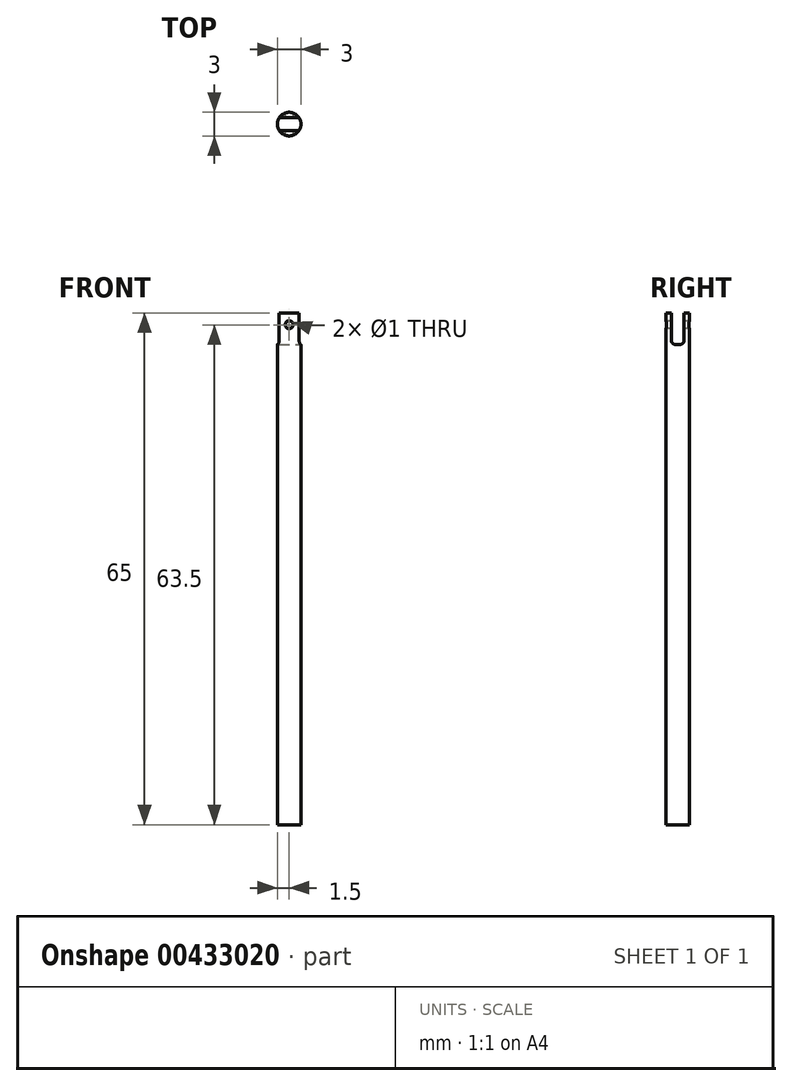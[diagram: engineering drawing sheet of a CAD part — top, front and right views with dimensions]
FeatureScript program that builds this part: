
annotation { "Feature Type Name" : "Feature", "Feature Type Description" : "" }
export const myFeature = defineFeature(function(context is Context, id is Id, definition is map)
    precondition{}
    {
        {
            var Q0;
            Q0=qCreatedBy(makeId("Top.planeOp"),FACE);
            var sketch = newSketch(context, id + "F0", { "sketchPlane" : qUnion([Q0])});
            skCircle(sketch, "E0", {"center": v(0, 0) * mm, "radius": 1.5 * mm});
            skSolve(sketch);
        }
        {
            var Q0;
            Q0=makeQuery(id+"F0.imprint","IMPRINT",FACE,{"disambiguationData":[TD([[makeQuery(id+"F0.imprint","IMPRINT",EDGE,{"derivedFrom":sQuery(id+"F0.wireOp",EDGE,"E0")}),1.0]])]});
            extrude(context, id + "F1", {"entities" : qUnion([Q0]), "offsetDistance" : 25 * mm, "depth" : 65 * mm});
        }
        {
            var Q0;
            Q0=makeQuery(id+"F1.opExtrude","CAP_FACE",FACE,{"disambiguationData":[OSD([sQuery(id+"F0.wireOp",EDGE,"E0")])],"isStart":false});
            var sketch = newSketch(context, id + "F2", { "sketchPlane" : qUnion([Q0])});
            skLineSegment(sketch, "E1", {"start": v(-1.27, 0.8) * mm, "end": v(1.27, 0.8) * mm});
            skLineSegment(sketch, "E2.MirrorCS", {"start": v(-1.27, -0.8) * mm, "end": v(1.27, -0.8) * mm});
            skSolve(sketch);
        }
        {
            var Q0;
            {var subQ0=sQuery(id+"F2.wireOp",EDGE,"E1");Q0=makeQuery(id+"F2.imprint","IMPRINT",FACE,{"disambiguationData":[TD([[makeQuery(id+"F2.imprint","IMPRINT",EDGE,{"derivedFrom":subQ0}),-1.0]])]});}
            extrude(context, id + "F3", {"entities" : qUnion([Q0]), "operationType" : NewBodyOperationType.REMOVE, "oppositeDirection" : true, "depth" : 4 * mm});
        }
        {
            var Q0;
            Q0=qCreatedBy(makeId("Front.planeOp"),FACE);
            var sketch = newSketch(context, id + "F4", { "sketchPlane" : qUnion([Q0])});
            skPoint(sketch, "E3", {"position": v(0, 63.5) * mm});
            skCircle(sketch, "E4", {"center": v(0, 63.5) * mm, "radius": 0.5 * mm});
            skSolve(sketch);
        }
        {
            var Q0;
            Q0=makeQuery(id+"F4.imprint","IMPRINT",FACE,{"disambiguationData":[TD([[makeQuery(id+"F4.imprint","IMPRINT",EDGE,{"derivedFrom":sQuery(id+"F4.wireOp",EDGE,"E4")}),1.0]])]});
            extrude(context, id + "F5", {"entities" : qUnion([Q0]), "operationType" : NewBodyOperationType.REMOVE, "oppositeDirection" : true, "depth" : 3 * mm, "symmetric" : true});
        }
        {
            var Q0;
            Q0=makeQuery(id+"F3.boolean.opBoolean","COPY",EDGE,{"derivedFrom":makeQuery(id+"F3.opExtrude","CAP_EDGE",EDGE,{"disambiguationData":[OSD([sQuery(id+"F2.wireOp",EDGE,"E2.MirrorCS")])],"isStart":false})});
            var Q1;
            Q1=makeQuery(id+"F3.boolean.opBoolean","COPY",EDGE,{"derivedFrom":makeQuery(id+"F3.opExtrude","CAP_EDGE",EDGE,{"disambiguationData":[OSD([sQuery(id+"F2.wireOp",EDGE,"E1")])],"isStart":false})});
            fillet(context, id + "F6", {"entities" : qUnion([Q0, Q1]), "radius" : 0.5 * mm, "tangentPropagation" : true, "allowEdgeOverflow" : false});
        }
    });
